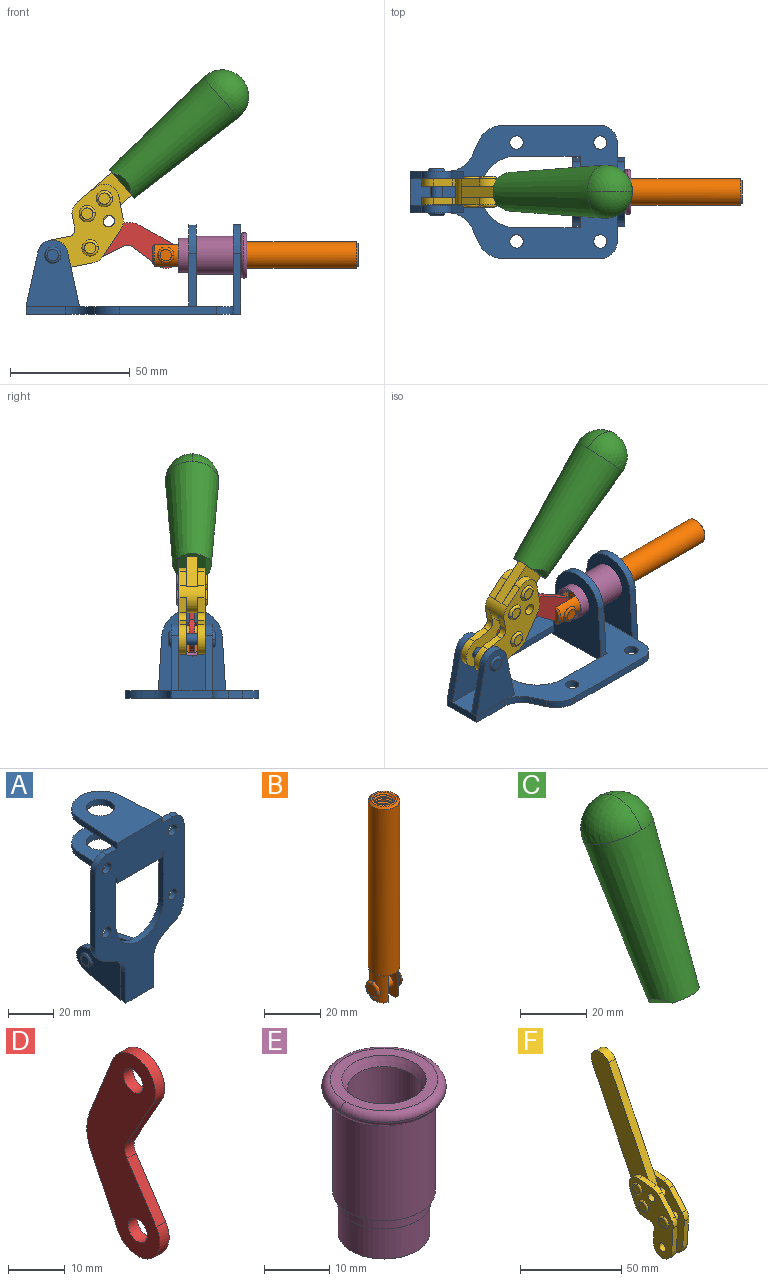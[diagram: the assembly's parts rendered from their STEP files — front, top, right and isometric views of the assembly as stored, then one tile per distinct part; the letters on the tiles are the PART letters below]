
ASSEMBLY  parts=6 mates=6
PART A: 55 faces, bbox 55.7x37.4x89.8 mm
  f0: torus R=2.41mm, axis (-1,0,0), area 15mm2, adj f11,f15,f25
  f1: torus R=2.41mm, axis (-1,0,0), area 15mm2, adj f10,f12,f22
  f2: cylinder r=2.78mm len=5.56mm, axis (0,-1,0), area 54.2mm2, adj f30,f54
  f3: cylinder r=14.99mm len=29.97mm, axis (0,-1,0), area 145.9mm2, adj f30,f49,f53,f54
  f4: cylinder r=2.78mm len=5.56mm, axis (0,-1,0), area 54.2mm2, adj f30,f54
  f5: cylinder r=2.78mm len=5.56mm, axis (0,-1,0), area 54.2mm2, adj f30,f54
  f6: cylinder r=2.78mm len=5.56mm, axis (0,-1,0), area 54.2mm2, adj f30,f54
  f7: cylinder r=6.35mm len=12.7mm, axis (0,0,1), area 123.6mm2, adj f27,f51
  f8: cylinder r=6.35mm len=12.7mm, axis (0,0,-1), area 124.7mm2, adj f21,f35
  f9: cylinder r=2.41mm len=11.18mm, axis (-1,0,0), area 169.4mm2, adj f16,f19
  f10: plane 4.83x4.83mm, normal (1,0,0), area 18.3mm2, adj f1,f12
  f11: plane 4.83x4.83mm, normal (-1,0,0), area 18.3mm2, adj f0,f15
  f12: torus R=2.41mm, axis (-1,0,0), area 15mm2, adj f1,f10,f22
  f13: cylinder r=6.35mm len=12.41mm, axis (1,0,0), area 53.4mm2, adj f18,f19,f22,f23
  f14: cylinder r=6.35mm len=12.41mm, axis (-1,0,0), area 53.4mm2, adj f16,f17,f24,f25
  f15: torus R=2.41mm, axis (-1,0,0), area 15mm2, adj f0,f11,f25
  f16: plane 27.86x22.35mm, normal (1,0,0), area 425.4mm2, adj f9,f14,f17,f24,f30
  f17: plane 22.86x4.97mm, normal (0,0.21,0.98), area 72.5mm2, adj f14,f16,f25,f30
  f18: plane 22.86x4.97mm, normal (0,0.21,0.98), area 72.5mm2, adj f13,f19,f22,f30
  f19: plane 27.86x22.35mm, normal (-1,0,0), area 425.4mm2, adj f9,f13,f18,f23,f30
  f20: cylinder r=12.7mm len=25.35mm, axis (0,0,-1), area 119.8mm2, adj f21,f34,f35,f36
  f21: plane 34.21x28.07mm, normal (0,0,-1), area 702.4mm2, adj f8,f20,f30,f34,f36
  f22: plane 27.96x22.45mm, normal (1,0,0), area 407.2mm2, adj f1,f12,f13,f18,f23,f30,f42,f43
  f23: plane 22.86x4.97mm, normal (0,0.21,-0.98), area 72.5mm2, adj f13,f19,f22,f44
  f24: plane 22.86x4.97mm, normal (0,0.21,-0.98), area 72.5mm2, adj f14,f16,f25,f44
  f25: plane 27.86x22.35mm, normal (-1,0,0), area 407.1mm2, adj f0,f14,f15,f17,f24,f30,f45,f46
  f26: plane 3.1x0.95mm, normal (0,0,-1), area 2.7mm2, adj f30,f49,f50,f54
  f27: plane 34.21x28.07mm, normal (0,0,1), area 702.4mm2, adj f7,f28,f30,f50,f52
  f28: cylinder r=12.7mm len=25.35mm, axis (0,0,1), area 118.8mm2, adj f27,f50,f51,f52
  f29: plane 3.1x0.95mm, normal (0,0,-1), area 2.7mm2, adj f30,f52,f53,f54
  f30: plane 86.54x55.63mm, normal (0,1,0), area 2362.9mm2, adj f2,f3,f4,f5,f6,f16,f17,f18
  f31: plane 40.56x3.1mm, normal (-1,0,0), area 125.7mm2, adj f30,f32,f48,f54
  f32: cylinder r=7.11mm len=7.11mm, axis (0,-1,0), area 34.6mm2, adj f30,f31,f33,f54
  f33: plane 6.67x3.1mm, normal (0,0,1), area 20.4mm2, adj f30,f32,f34,f54
  f34: plane 25.39x3.13mm, normal (-1,0.06,0), area 79.5mm2, adj f20,f21,f33,f35,f54
  f35: plane 37.31x28.45mm, normal (0,0,1), area 789.9mm2, adj f8,f20,f34,f36,f54
  f36: plane 25.39x3.13mm, normal (1,0.06,0), area 79.5mm2, adj f20,f21,f35,f37,f54
  f37: plane 6.67x3.1mm, normal (0,0,1), area 20.4mm2, adj f30,f36,f38,f54
  f38: cylinder r=7.11mm len=7.11mm, axis (0,-1,0), area 34.6mm2, adj f30,f37,f39,f54
  f39: plane 40.56x3.1mm, normal (1,0,0), area 125.7mm2, adj f30,f38,f40,f54
  f40: cylinder r=11.18mm len=10.16mm, axis (0,-1,0), area 39.5mm2, adj f30,f39,f41,f54
  f41: plane 6.09x3.1mm, normal (0.42,0,-0.91), area 20.8mm2, adj f30,f40,f42,f54
  f42: cylinder r=11.18mm len=9.41mm, axis (0,-1,0), area 37.2mm2, adj f22,f30,f41,f43,f54
  f43: plane 16.5x3.1mm, normal (1,0,0), area 51.1mm2, adj f22,f42,f44,f54
  f44: plane 17.37x3.1mm, normal (0,0,-1), area 53.8mm2, adj f23,f24,f30,f43,f45,f54
  f45: plane 16.5x3.1mm, normal (-1,0,0), area 51.1mm2, adj f25,f44,f46,f54
  f46: cylinder r=11.18mm len=9.41mm, axis (0,-1,0), area 37.2mm2, adj f25,f30,f45,f47,f54
  f47: plane 6.09x3.1mm, normal (-0.42,0,-0.91), area 20.8mm2, adj f30,f46,f48,f54
  f48: cylinder r=11.18mm len=10.16mm, axis (0,-1,0), area 39.5mm2, adj f30,f31,f47,f54
  f49: plane 26.54x3.1mm, normal (-1,0,0), area 82.3mm2, adj f3,f26,f30,f54
  f50: plane 25.39x3.1mm, normal (1,0.06,0), area 78.8mm2, adj f26,f27,f28,f51,f54
  f51: plane 37.31x28.45mm, normal (0,0,-1), area 789.9mm2, adj f7,f28,f50,f52,f54
  f52: plane 25.39x3.1mm, normal (-1,0.06,0), area 78.8mm2, adj f27,f28,f29,f51,f54
  f53: plane 26.54x3.1mm, normal (1,0,0), area 82.3mm2, adj f3,f29,f30,f54
  f54: plane 89.66x55.63mm, normal (0,-1,0), area 2678.5mm2, adj f2,f3,f4,f5,f6,f26,f29,f31
PART B: 48 faces, bbox 12.6x11.1x86.1 mm
  f0: torus R=2.41mm, axis (-1,0,0), area 15mm2, adj f30,f32,f34
  f1: torus R=2.41mm, axis (-1,0,0), area 15mm2, adj f29,f31,f33
  f2: cylinder r=5.54mm len=72.39mm, axis (0,0,1), area 2518.5mm2, adj f3,f4,f42,f43
  f3: cone r=5.54mm half-angle=45deg, axis (0,0,1), area 7.6mm2, adj f2,f5,f41
  f4: cone r=5.54mm half-angle=45deg, axis (0,0,-1), area 34.9mm2, adj f2,f39
  f5: cylinder r=5.08mm len=11.48mm, axis (0,0,1), area 108.3mm2, adj f3,f7,f8,f41
  f6: cylinder r=2.41mm len=4.83mm, axis (-1,0,0), area 71.2mm2, adj f40,f41
  f7: cylinder r=2.41mm len=4.83mm, axis (-1,0,0), area 7.6mm2, adj f5,f34
  f8: cone r=5.08mm half-angle=45deg, axis (0,0,1), area 10.6mm2, adj f5,f37,f41
  f9: cone r=3.98mm half-angle=45deg, axis (0,0,1), area 17.6mm2, adj f27,f39,f45,f46,f47
  f10: cylinder r=2.41mm len=4.83mm, axis (-1,0,0), area 7.6mm2, adj f33,f38
  f11: cylinder r=3.2mm len=6.4mm, axis (0,0,1), area 78.4mm2, adj f12,f28,f44,f45,f47
  f12: cylinder r=3.2mm len=6.4mm, axis (0,0,1), area 10.5mm2, adj f11,f13,f45,f47
  f13: cylinder r=3.2mm len=6.4mm, axis (0,0,1), area 10.5mm2, adj f12,f14,f45,f47
  f14: cylinder r=3.2mm len=6.4mm, axis (0,0,1), area 10.5mm2, adj f13,f15,f45,f47
  f15: cylinder r=3.2mm len=6.4mm, axis (0,0,1), area 10.5mm2, adj f14,f16,f45,f47
  f16: cylinder r=3.2mm len=6.4mm, axis (0,0,1), area 10.5mm2, adj f15,f17,f45,f47
  f17: cylinder r=3.2mm len=6.4mm, axis (0,0,1), area 10.5mm2, adj f16,f18,f45,f47
  f18: cylinder r=3.2mm len=6.4mm, axis (0,0,1), area 10.5mm2, adj f17,f19,f45,f47
  f19: cylinder r=3.2mm len=6.4mm, axis (0,0,1), area 10.5mm2, adj f18,f20,f45,f47
  f20: cylinder r=3.2mm len=6.4mm, axis (0,0,1), area 10.5mm2, adj f19,f21,f45,f47
  f21: cylinder r=3.2mm len=6.4mm, axis (0,0,1), area 10.5mm2, adj f20,f22,f45,f47
  f22: cylinder r=3.2mm len=6.4mm, axis (0,0,1), area 10.5mm2, adj f21,f23,f45,f47
  f23: cylinder r=3.2mm len=6.4mm, axis (0,0,1), area 10.5mm2, adj f22,f24,f45,f47
  f24: cylinder r=3.2mm len=6.4mm, axis (0,0,1), area 10.5mm2, adj f23,f25,f45,f47
  f25: cylinder r=3.2mm len=6.4mm, axis (0,0,1), area 10.5mm2, adj f24,f26,f45,f47
  f26: cylinder r=3.2mm len=6.4mm, axis (0,0,1), area 10.5mm2, adj f25,f27,f45,f47
  f27: cylinder r=3.2mm len=6.4mm, axis (0,0,1), area 7.4mm2, adj f9,f26,f45,f47
  f28: cone r=3.2mm half-angle=60deg, axis (0,0,1), area 37.2mm2, adj f11
  f29: plane 4.83x4.83mm, normal (-1,0,0), area 18.3mm2, adj f1,f31
  f30: plane 4.83x4.83mm, normal (1,0,0), area 18.3mm2, adj f0,f32
  f31: torus R=2.41mm, axis (-1,0,0), area 15mm2, adj f1,f29,f33
  f32: torus R=2.41mm, axis (-1,0,0), area 15mm2, adj f0,f30,f34
  f33: plane 6.83x6.83mm, normal (1,0,0), area 18.3mm2, adj f1,f10,f31
  f34: plane 6.83x6.83mm, normal (-1,0,0), area 18.3mm2, adj f0,f7,f32
  f35: cone r=5.08mm half-angle=45deg, axis (0,0,1), area 10.6mm2, adj f36,f38,f40
  f36: plane 7.25x1.97mm, normal (0,0,-1), area 10mm2, adj f35,f40
  f37: plane 7.25x1.97mm, normal (0,0,-1), area 10mm2, adj f8,f41
  f38: cylinder r=5.08mm len=11.48mm, axis (0,0,1), area 108.3mm2, adj f10,f35,f40,f42
  f39: plane 9.55x9.55mm, normal (0,0,1), area 22mm2, adj f4,f9
  f40: plane 12.76x10.09mm, normal (1,0,0), area 95.7mm2, adj f6,f35,f36,f38,f42,f43
  f41: plane 12.76x10.09mm, normal (-1,0,0), area 95.7mm2, adj f3,f5,f6,f8,f37,f43
  f42: cone r=5.54mm half-angle=45deg, axis (0,0,1), area 7.6mm2, adj f2,f38,f40
  f43: plane 11.07x4.7mm, normal (0,0,-1), area 50.4mm2, adj f2,f40,f41
  f44: plane 0.89x0.62mm, normal (-1,0,0), area 0.3mm2, adj f11,f45,f46,f47
  f45: bspline ~24.8x7.63mm, area 266.6mm2, adj f9,f11,f12,f13,f14,f15,f16,f17
  f46: bspline ~24.87x7.63mm, area 73.6mm2, adj f9,f44,f45,f47
  f47: bspline ~24.98x7.63mm, area 272.5mm2, adj f9,f11,f12,f13,f14,f15,f16,f17
PART C: 11 faces, bbox 22.3x42.6x64.5 mm
  f0: sphere r=11.13mm, area 411.4mm2, adj f1,f8
  f1: cone r=11.11mm half-angle=3.3deg, axis (0,0.44,0.9), area 3251.8mm2, adj f0,f7,f8,f9,f10
  f2: cylinder r=6.16mm len=11.7mm, axis (1,0,0), area 89.5mm2, adj f3,f4,f5,f6
  f3: plane 60.23x36.75mm, normal (-1,0,0), area 763.6mm2, adj f2,f4,f6,f10
  f4: plane 51.37x25.05mm, normal (0,0.9,-0.44), area 264.2mm2, adj f2,f3,f5,f10
  f5: plane 60.23x36.75mm, normal (1,0,0), area 763.6mm2, adj f2,f4,f6,f10
  f6: plane 51.37x25.05mm, normal (0,-0.9,0.44), area 264.2mm2, adj f2,f3,f5,f10
  f7: plane 9.95x5.95mm, normal (0.71,-0.31,-0.64), area 25.8mm2, adj f1,f10
  f8: sphere r=11.13mm, area 411.4mm2, adj f0,f1
  f9: plane 9.95x5.95mm, normal (-0.71,-0.31,-0.64), area 25.8mm2, adj f1,f10
  f10: plane 14.27x11.38mm, normal (0,-0.44,-0.9), area 106.7mm2, adj f1,f3,f4,f5,f6,f7,f9
PART D: 12 faces, bbox 2.3x18.2x42.8 mm
  f0: cylinder r=2.4mm len=4.8mm, axis (1,0,0), area 34.9mm2, adj f4,f11
  f1: cylinder r=10.41mm len=8.47mm, axis (1,0,0), area 20.2mm2, adj f4,f9,f10,f11
  f2: cylinder r=3.05mm len=3.16mm, axis (1,0,0), area 7.7mm2, adj f4,f6,f7,f11
  f3: cylinder r=2.4mm len=4.8mm, axis (1,0,0), area 34.9mm2, adj f4,f11
  f4: plane 42.81x18.23mm, normal (-1,0,0), area 414.1mm2, adj f0,f1,f2,f3,f5,f6,f7,f8
  f5: cylinder r=5.54mm len=10.67mm, axis (1,0,0), area 41.8mm2, adj f4,f6,f10,f11
  f6: plane 11.66x6.53mm, normal (0,-0.87,-0.49), area 30.9mm2, adj f2,f4,f5,f11
  f7: plane 11.17x7.33mm, normal (0,-0.84,0.55), area 30.9mm2, adj f2,f4,f8,f11
  f8: cylinder r=5.54mm len=10.51mm, axis (1,0,0), area 41.8mm2, adj f4,f7,f9,f11
  f9: plane 13.67x6.67mm, normal (0,0.9,-0.44), area 35.1mm2, adj f1,f4,f8,f11
  f10: plane 14.1x5.7mm, normal (0,0.93,0.37), area 35.1mm2, adj f1,f4,f5,f11
  f11: plane 42.81x18.23mm, normal (1,0,0), area 414.1mm2, adj f0,f1,f2,f3,f5,f6,f7,f8
PART E: 15 faces, bbox 20.6x20.6x28.7 mm
  f0: torus R=8.26mm, axis (0,0,1), area 56.8mm2, adj f1,f10,f12
  f1: torus R=8.26mm, axis (0,0,1), area 56.8mm2, adj f0,f6,f13
  f2: cylinder r=5.59mm len=25.91mm, axis (0,0,1), area 909.6mm2, adj f3,f4
  f3: cone r=6.86mm half-angle=45deg, axis (0,0,-1), area 70.2mm2, adj f2,f14
  f4: cone r=6.47mm half-angle=30deg, axis (0,0,1), area 66.7mm2, adj f2,f13
  f5: cylinder r=7.04mm len=14.07mm, axis (0,0,1), area 252.6mm2, adj f11,f14
  f6: torus R=8.26mm, axis (0,0,1), area 56.8mm2, adj f1,f12,f13
  f7: cylinder r=7.16mm len=14.33mm, axis (0,0,1), area 91.5mm2, adj f9,f11
  f8: cylinder r=7.86mm len=18.42mm, axis (0,0,1), area 909.6mm2, adj f9,f10
  f9: plane 15.72x15.72mm, normal (0,0,-1), area 33mm2, adj f7,f8
  f10: plane 16.51x16.51mm, normal (0,0,-1), area 19.9mm2, adj f0,f8,f12
  f11: plane 14.33x14.33mm, normal (0,0,-1), area 5.7mm2, adj f5,f7
  f12: torus R=8.26mm, axis (0,0,1), area 56.8mm2, adj f0,f6,f10
  f13: plane 16.51x16.51mm, normal (0,0,1), area 82.7mm2, adj f1,f4,f6
  f14: plane 14.07x14.07mm, normal (0,0,-1), area 7.8mm2, adj f3,f5
PART F: 59 faces, bbox 12.9x60.2x99.6 mm
  f0: torus R=2.39mm, axis (-1,0,0), area 14.9mm2, adj f20,f43,f51
  f1: torus R=2.39mm, axis (-1,0,0), area 14.9mm2, adj f19,f42,f51
  f2: torus R=2.39mm, axis (-1,0,0), area 14.9mm2, adj f18,f35,f51
  f3: torus R=2.39mm, axis (-1,0,0), area 14.9mm2, adj f14,f17,f23
  f4: torus R=2.39mm, axis (-1,0,0), area 14.9mm2, adj f13,f16,f23
  f5: torus R=2.39mm, axis (-1,0,0), area 14.9mm2, adj f12,f15,f23
  f6: cylinder r=2.39mm len=4.78mm, axis (1,0,0), area 46.5mm2, adj f48,f50,f51
  f7: cylinder r=2.39mm len=4.78mm, axis (1,0,0), area 46.5mm2, adj f50,f51
  f8: cylinder r=6.35mm len=12.68mm, axis (1,0,0), area 61.8mm2, adj f38,f39,f50,f51
  f9: cylinder r=2.39mm len=4.78mm, axis (-1,0,0), area 70.5mm2, adj f46,f50
  f10: cylinder r=2.39mm len=4.78mm, axis (-1,0,0), area 46.5mm2, adj f23,f45,f46
  f11: cylinder r=2.39mm len=4.78mm, axis (-1,0,0), area 46.5mm2, adj f23,f46
  f12: plane 4.78x4.78mm, normal (1,0,0), area 17.9mm2, adj f5,f15
  f13: plane 4.78x4.78mm, normal (1,0,0), area 17.9mm2, adj f4,f16
  f14: plane 4.78x4.78mm, normal (1,0,0), area 17.9mm2, adj f3,f17
  f15: torus R=2.39mm, axis (-1,0,0), area 14.9mm2, adj f5,f12,f23
  f16: torus R=2.39mm, axis (-1,0,0), area 14.9mm2, adj f4,f13,f23
  f17: torus R=2.39mm, axis (-1,0,0), area 14.9mm2, adj f3,f14,f23
  f18: plane 4.78x4.78mm, normal (-1,0,0), area 17.9mm2, adj f2,f35
  f19: plane 4.78x4.78mm, normal (-1,0,0), area 17.9mm2, adj f1,f42
  f20: plane 4.78x4.78mm, normal (-1,0,0), area 17.9mm2, adj f0,f43
  f21: plane 2.26x0.2mm, normal (1,0,0), area 0.2mm2, adj f31,f44
  f22: plane 2.26x0.2mm, normal (-1,0,0), area 0.2mm2, adj f41,f44
  f23: plane 39.37x30.77mm, normal (1,0,0), area 565.5mm2, adj f3,f4,f5,f10,f11,f15,f16,f17
  f24: cylinder r=6.1mm len=4.15mm, axis (-1,0,0), area 14.7mm2, adj f23,f25,f32,f46
  f25: plane 10.25x9.01mm, normal (0,-0.75,0.66), area 42.3mm2, adj f23,f24,f26,f46
  f26: cylinder r=6.35mm len=4.64mm, axis (-1,0,0), area 15.6mm2, adj f23,f25,f27,f46
  f27: plane 15.84x3.1mm, normal (0,-1,-0.07), area 49.2mm2, adj f23,f26,f28,f46
  f28: cylinder r=6.35mm len=12.68mm, axis (-1,0,0), area 61.8mm2, adj f23,f27,f29,f46
  f29: plane 8.11x3.1mm, normal (0,1,0.07), area 25.2mm2, adj f23,f28,f30,f46
  f30: cylinder r=3.05mm len=3.25mm, axis (-1,0,0), area 14.8mm2, adj f23,f29,f31,f46
  f31: plane 5.99x3.1mm, normal (0,0.07,-1), area 18.6mm2, adj f21,f23,f30,f44,f46
  f32: plane 9.5x3.1mm, normal (0,-0.07,1), area 29.5mm2, adj f23,f24,f33,f46,f47
  f33: cylinder r=6.1mm len=8.63mm, axis (-1,0,0), area 39.1mm2, adj f23,f32,f34,f47
  f34: plane 8.65x3.96mm, normal (0,0.91,-0.42), area 29.5mm2, adj f23,f33,f44,f47
  f35: torus R=2.39mm, axis (-1,0,0), area 14.9mm2, adj f2,f18,f51
  f36: plane 10.25x9.01mm, normal (0,-0.75,0.66), area 42.3mm2, adj f37,f49,f50,f51
  f37: cylinder r=6.35mm len=4.64mm, axis (1,0,0), area 15.6mm2, adj f36,f38,f50,f51
  f38: plane 15.84x3.1mm, normal (0,-1,-0.07), area 49.2mm2, adj f8,f37,f50,f51
  f39: plane 8.11x3.1mm, normal (0,1,0.07), area 25.2mm2, adj f8,f40,f50,f51
  f40: cylinder r=3.05mm len=3.25mm, axis (1,0,0), area 14.8mm2, adj f39,f41,f50,f51
  f41: plane 5.99x3.1mm, normal (0,0.07,-1), area 18.6mm2, adj f22,f40,f44,f50,f51
  f42: torus R=2.39mm, axis (-1,0,0), area 14.9mm2, adj f1,f19,f51
  f43: torus R=2.39mm, axis (-1,0,0), area 14.9mm2, adj f0,f20,f51
  f44: cylinder r=6.35mm len=12.12mm, axis (-1,0,0), area 128.9mm2, adj f21,f22,f23,f31,f34,f41,f46,f47
  f45: plane 2.65x1.35mm, normal (1,0,0), area 1mm2, adj f10,f55
  f46: plane 39.08x20.42mm, normal (-1,0,0), area 412.5mm2, adj f9,f10,f11,f24,f25,f26,f27,f28
  f47: plane 77.62x39.82mm, normal (1,0,0), area 850mm2, adj f32,f33,f34,f44,f53,f54,f55
  f48: plane 2.65x1.35mm, normal (-1,0,0), area 1mm2, adj f6,f55
  f49: cylinder r=6.1mm len=4.15mm, axis (1,0,0), area 14.7mm2, adj f36,f50,f51,f56
  f50: plane 39.08x20.42mm, normal (1,0,0), area 412.5mm2, adj f6,f7,f8,f9,f36,f37,f38,f39
  f51: plane 39.37x30.77mm, normal (-1,0,0), area 565.5mm2, adj f0,f1,f2,f6,f7,f8,f35,f36
  f52: plane 8.65x3.96mm, normal (0,0.91,-0.42), area 29.5mm2, adj f44,f51,f57,f58
  f53: plane 68.49x33.4mm, normal (0,0.9,-0.44), area 358.1mm2, adj f44,f47,f54,f58
  f54: cylinder r=6.35mm len=12.06mm, axis (1,0,0), area 93.7mm2, adj f47,f53,f55,f58
  f55: plane 68.49x33.4mm, normal (0,-0.9,0.44), area 358.1mm2, adj f44,f45,f46,f47,f48,f50,f54,f58
  f56: plane 9.5x3.1mm, normal (0,-0.07,1), area 29.5mm2, adj f49,f50,f51,f57,f58
  f57: cylinder r=6.1mm len=8.63mm, axis (1,0,0), area 39.1mm2, adj f51,f52,f56,f58
  f58: plane 77.62x39.82mm, normal (-1,0,0), area 850mm2, adj f44,f52,f53,f54,f55,f56,f57
PLACE A rot(axis=(0.58,0.58,0.58),120deg) t=(0,0,0)mm fixed
PLACE B rot(axis=(-0.58,0.58,-0.58),120deg) t=(-0.38,0,49.23)mm
PLACE C rot(axis=(0.52,0.52,0.68),111.8deg) t=(5.28,-0.04,9.14)mm
PLACE D rot(axis=(0.57,-0.57,-0.6),118deg) t=(-2.56,0,2.14)mm
PLACE E rot(axis=(0,1,0),90deg) t=(0,-24.61,24.61)mm
PLACE F rot(axis=(0.52,0.52,0.68),111.8deg) t=(5.28,0,9.14)mm
MATE revolute D.f3 <-> B.f6  axis (0,-1,0) through (15.1,0,24.61)mm
MATE fastened C.f2 <-> F.f54  axis (0,1,0) through (39.8,-2.35,91.94)mm
MATE revolute D.f5 <-> F.f4  axis (0,-1,0) through (-16.51,0,27.64)mm
MATE slider B.f2 <-> E.f2  axis (1,0,0) through (58.4,0,24.61)mm
MATE revolute A.f0 <-> F.f7  axis (0,-1,0) through (-32.09,0,24.61)mm
MATE fastened E.f2 <-> A.f7  axis (-1,0,0) through (46.39,0,24.61)mm
